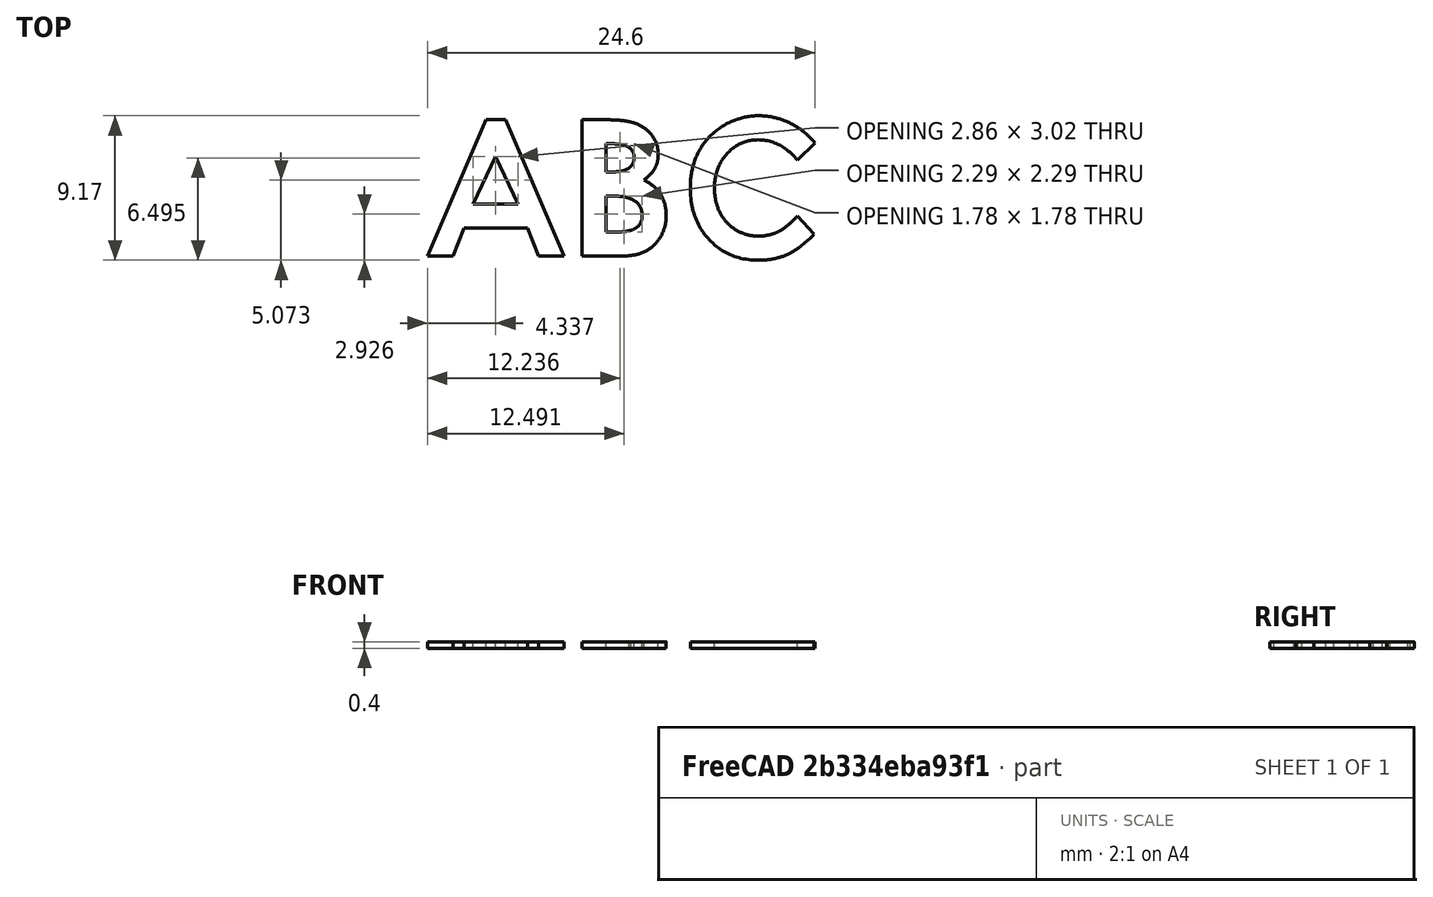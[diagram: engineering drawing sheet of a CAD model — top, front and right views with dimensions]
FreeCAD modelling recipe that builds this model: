
FCSTD DOCUMENT  (FreeCAD 0.20R29410 (Git))
Label: TxtExtrude
License: All rights reserved
LicenseURL: http://en.wikipedia.org/wiki/All_rights_reserved
objects: Part::FeaturePython×2, App::DocumentObjectGroup×2, Part::Part2DObjectPython×1, Part::Extrusion×1
note: 4 computed .brp shape members not serialized (recipe doc carries the construction recipe); baked Part::Feature solids carry a one-line shape summary decoded from their .brp

FEATURE [Part::Part2DObjectPython] ShapeString  # Draft 2D object (typed FeaturePython)
  FontFile = <path>
  MakeFace = true
  Placement = pos=(-12.66,-4.33,0) rot=(0,0,1;0rad)
  Size = 10
  String = ABC
  Tracking = 0
FEATURE [Part::FeaturePython] NPointsPoint_P  # WARN: FeaturePython — macro-defined, semantics opaque (R4)
  Parametric = 0
  Points = -> [ShapeString]
  X = 12.6643
  Y = 0.698925
  Z = 0
FEATURE [Part::FeaturePython] NPointsPoint_P001  # WARN: FeaturePython — macro-defined, semantics opaque (R4)
  Parametric = 0
  Points = -> [ShapeString]
  X = 21.4138
  Y = 4.33294
  Z = 0
FEATURE [App::DocumentObjectGroup] WorkPoints_P
  Group = -> [NPointsPoint_P,NPointsPoint_P001]
FEATURE [App::DocumentObjectGroup] WorkFeatures
  Group = -> [WorkPoints_P]
FEATURE [Part::Extrusion] Extrude
  Base = -> ShapeString
  Dir = (0,0,1)
  DirMode = 2
  FaceMakerClass = Part::FaceMakerBullseye
  LengthFwd = 0.4
  LengthRev = 0
  Solid = false
  Symmetric = false
note: 1 file-system path scrubbed to <path> (originals preserved in the JSON sidecar)
